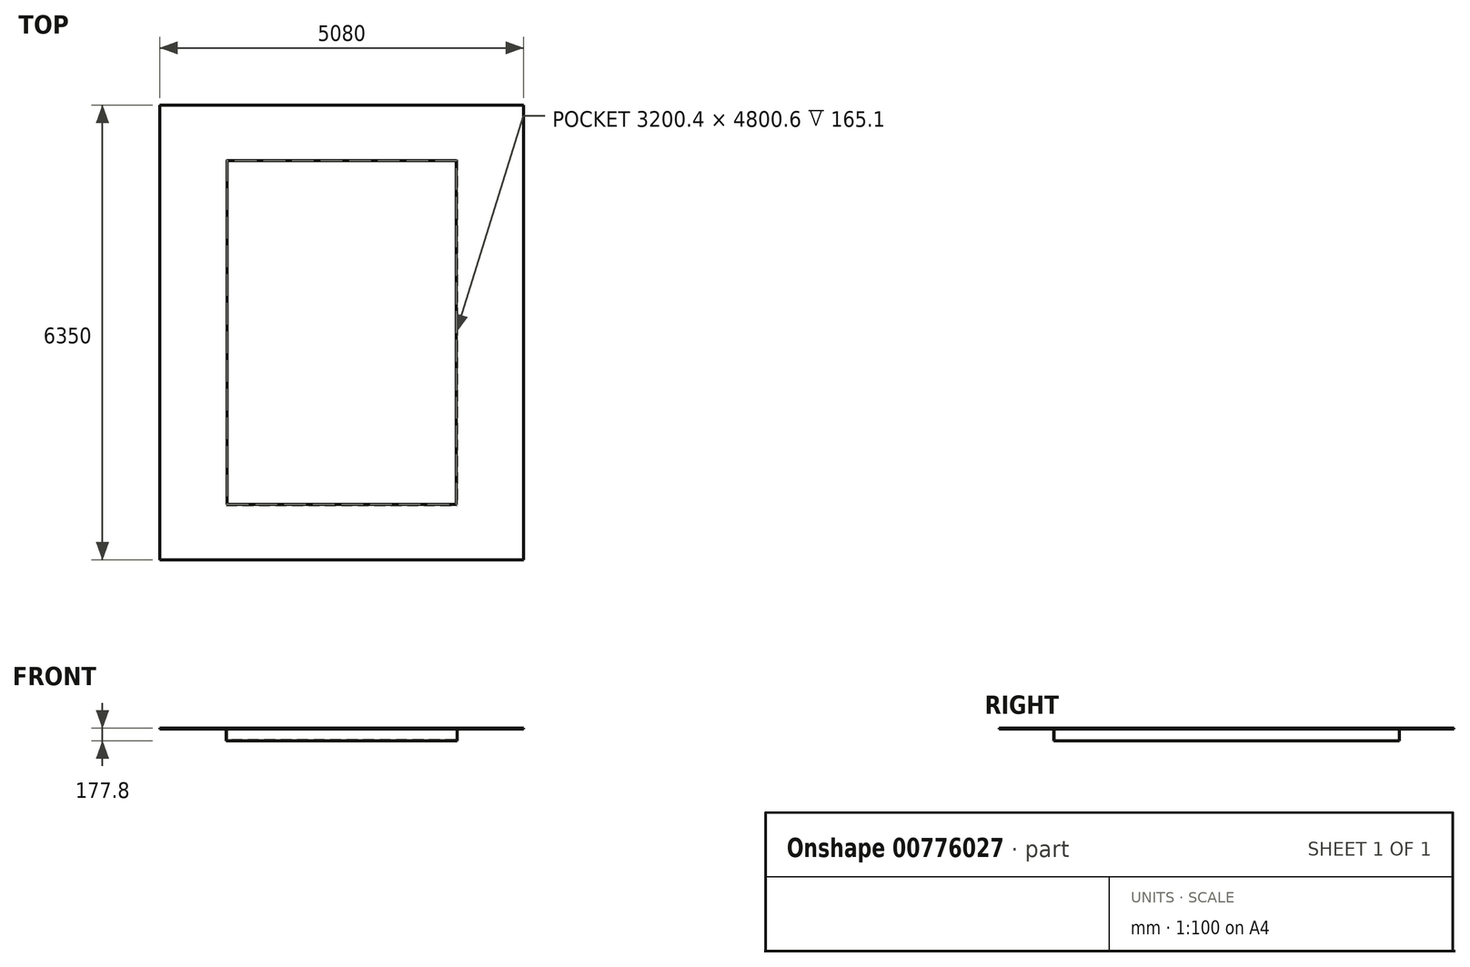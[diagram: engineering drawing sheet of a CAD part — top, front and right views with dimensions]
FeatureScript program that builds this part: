
annotation { "Feature Type Name" : "Feature", "Feature Type Description" : "" }
export const myFeature = defineFeature(function(context is Context, id is Id, definition is map)
    precondition{}
    {
        {
            var Q0;
            Q0=qCreatedBy(makeId("Top.planeOp"),FACE);
            var sketch = newSketch(context, id + "F0", { "sketchPlane" : qUnion([Q0])});
            skLineSegment(sketch, "E0.bottom", {"start": v(1600.2, -2400.3) * mm, "end": v(-1600.2, -2400.3) * mm});
            skLineSegment(sketch, "E0.top", {"start": v(1600.2, 2400.3) * mm, "end": v(-1600.2, 2400.3) * mm});
            skLineSegment(sketch, "E0.left", {"start": v(1600.2, -2400.3) * mm, "end": v(1600.2, 2400.3) * mm});
            skLineSegment(sketch, "E0.right", {"start": v(-1600.2, -2400.3) * mm, "end": v(-1600.2, 2400.3) * mm});
            skPoint(sketch, "E0.middle", {"position": v(0, 0) * mm});
            skSolve(sketch);
        }
        {
            var Q0;
            Q0 = qSketchRegion(id + "F0", true);
            extrude(context, id + "F1", {"entities" : qUnion([Q0]), "depth" : 12.7 * mm, "offsetDistance" : 25.4 * mm});
        }
        {
            var Q0;
            Q0=qCreatedBy(makeId("Top.planeOp"),FACE);
            var sketch = newSketch(context, id + "F2", { "sketchPlane" : qUnion([Q0])});
            skLineSegment(sketch, "E1.bottom", {"start": v(1600.2, -2400.3) * mm, "end": v(-1600.2, -2400.3) * mm});
            skLineSegment(sketch, "E1.top", {"start": v(1600.2, 2400.3) * mm, "end": v(-1600.2, 2400.3) * mm});
            skLineSegment(sketch, "E1.left", {"start": v(1600.2, -2400.3) * mm, "end": v(1600.2, 2400.3) * mm});
            skLineSegment(sketch, "E1.right", {"start": v(-1600.2, -2400.3) * mm, "end": v(-1600.2, 2400.3) * mm});
            skPoint(sketch, "E1.middle", {"position": v(0, 0) * mm});
            skLineSegment(sketch, "E2.bottom", {"start": v(-1612.9, 2413) * mm, "end": v(1612.9, 2413) * mm});
            skLineSegment(sketch, "E2.top", {"start": v(-1612.9, -2413) * mm, "end": v(1612.9, -2413) * mm});
            skLineSegment(sketch, "E2.left", {"start": v(-1612.9, 2413) * mm, "end": v(-1612.9, -2413) * mm});
            skLineSegment(sketch, "E2.right", {"start": v(1612.9, 2413) * mm, "end": v(1612.9, -2413) * mm});
            skSolve(sketch);
        }
        {
            var Q0;
            Q0 = qSketchRegion(id + "F2", true);
            extrude(context, id + "F3", {"entities" : qUnion([Q0]), "operationType" : NewBodyOperationType.ADD, "depth" : 165.1 * mm, "offsetDistance" : 25.4 * mm});
        }
        {
            var Q0;
            Q0=qCreatedBy(makeId("Right.planeOp"),FACE);
            var sketch = newSketch(context, id + "F4", { "sketchPlane" : qUnion([Q0])});
            skLineSegment(sketch, "E3.bottom", {"start": v(-2413, 177.8) * mm, "end": v(2413, 177.8) * mm});
            skLineSegment(sketch, "E3.top", {"start": v(-2413, 165.1) * mm, "end": v(2413, 165.1) * mm});
            skLineSegment(sketch, "E3.left", {"start": v(-2413, 177.8) * mm, "end": v(-2413, 165.1) * mm});
            skLineSegment(sketch, "E3.right", {"start": v(2413, 177.8) * mm, "end": v(2413, 165.1) * mm});
            skPoint(sketch, "E3.middle", {"position": v(0, 171.45) * mm});
            skSolve(sketch);
        }
        {
            var Q0;
            Q0 = qSketchRegion(id + "F4", true);
            extrude(context, id + "F5", {"entities" : qUnion([Q0]), "operationType" : NewBodyOperationType.ADD, "endBound" : BoundingType.SYMMETRIC, "depth" : 5080 * mm, "offsetDistance" : 25.4 * mm});
        }
        {
            var Q0;
            Q0 = qSketchRegion(id + "F4", true);
            extrude(context, id + "F6", {"entities" : qUnion([Q0]), "operationType" : NewBodyOperationType.REMOVE, "endBound" : BoundingType.SYMMETRIC, "oppositeDirection" : true, "depth" : 3200.4 * mm, "offsetDistance" : 25.4 * mm});
        }
        {
            var Q0;
            Q0=qCreatedBy(makeId("Front.planeOp"),FACE);
            var sketch = newSketch(context, id + "F7", { "sketchPlane" : qUnion([Q0])});
            skLineSegment(sketch, "E4.bottom", {"start": v(-2540, 177.8) * mm, "end": v(2540, 177.8) * mm});
            skLineSegment(sketch, "E4.top", {"start": v(-2540, 165.1) * mm, "end": v(2540, 165.1) * mm});
            skLineSegment(sketch, "E4.left", {"start": v(-2540, 177.8) * mm, "end": v(-2540, 165.1) * mm});
            skLineSegment(sketch, "E4.right", {"start": v(2540, 177.8) * mm, "end": v(2540, 165.1) * mm});
            skPoint(sketch, "E4.middle", {"position": v(0, 171.45) * mm});
            skSolve(sketch);
        }
        {
            var Q0;
            Q0 = qSketchRegion(id + "F7", true);
            extrude(context, id + "F8", {"entities" : qUnion([Q0]), "operationType" : NewBodyOperationType.ADD, "endBound" : BoundingType.SYMMETRIC, "depth" : 6350 * mm, "offsetDistance" : 25.4 * mm});
        }
        {
            var Q0;
            Q0=qCreatedBy(makeId("Front.planeOp"),FACE);
            var sketch = newSketch(context, id + "F9", { "sketchPlane" : qUnion([Q0])});
            skLineSegment(sketch, "E5.bottom", {"start": v(-1600.2, 165.1) * mm, "end": v(1600.2, 165.1) * mm});
            skLineSegment(sketch, "E5.top", {"start": v(-1600.2, 177.8) * mm, "end": v(1600.2, 177.8) * mm});
            skLineSegment(sketch, "E5.left", {"start": v(-1600.2, 165.1) * mm, "end": v(-1600.2, 177.8) * mm});
            skLineSegment(sketch, "E5.right", {"start": v(1600.2, 165.1) * mm, "end": v(1600.2, 177.8) * mm});
            skPoint(sketch, "E5.middle", {"position": v(0, 171.45) * mm});
            skSolve(sketch);
        }
        {
            var Q0;
            Q0 = qSketchRegion(id + "F9", true);
            extrude(context, id + "F10", {"entities" : qUnion([Q0]), "operationType" : NewBodyOperationType.REMOVE, "endBound" : BoundingType.SYMMETRIC, "oppositeDirection" : true, "depth" : 4800.6 * mm, "offsetDistance" : 25.4 * mm});
        }
    });
